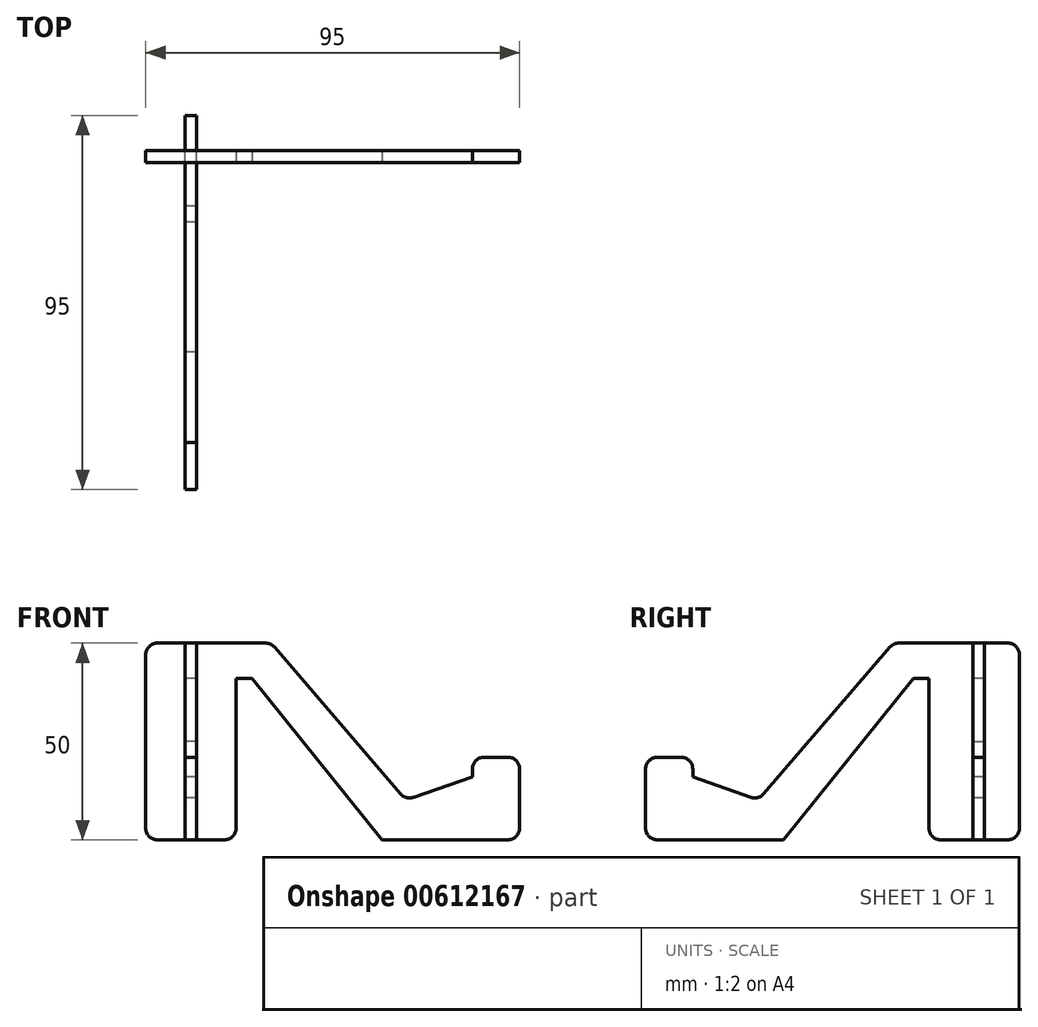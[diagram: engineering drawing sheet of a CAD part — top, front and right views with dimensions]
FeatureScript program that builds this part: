
annotation { "Feature Type Name" : "Feature", "Feature Type Description" : "" }
export const myFeature = defineFeature(function(context is Context, id is Id, definition is map)
    precondition{}
    {
        {
            assignVariable(context, id + "F0", {"name" : "thickness", "anyValue" : 3});
        }
        {
            var Q0;
            Q0=qCreatedBy(makeId("Right.planeOp"),FACE);
            var sketch = newSketch(context, id + "F1", { "sketchPlane" : qUnion([Q0])});
            skLineSegment(sketch, "E0", {"start": v(75, 0) * mm, "end": v(92, 0) * mm});
            skLineSegment(sketch, "E1", {"start": v(95, 3) * mm, "end": v(95, 47) * mm});
            skLineSegment(sketch, "E2", {"start": v(92, 50) * mm, "end": v(86.13, 50) * mm});
            skLineSegment(sketch, "E3", {"start": v(62.1, 48.96) * mm, "end": v(30, 11.67) * mm});
            skLineSegment(sketch, "E4", {"start": v(26.73, 10.8) * mm, "end": v(12, 16) * mm});
            skLineSegment(sketch, "E5", {"start": v(12, 16) * mm, "end": v(12, 18) * mm});
            skLineSegment(sketch, "E6", {"start": v(9, 21) * mm, "end": v(3, 21) * mm});
            skLineSegment(sketch, "E7", {"start": v(0, 18) * mm, "end": v(0, 3) * mm});
            skLineSegment(sketch, "E8", {"start": v(-17.73, 9.3) * mm, "end": v(124.5, 9.3) * mm, "construction": true});
            skLineSegment(sketch, "E9", {"start": v(35, 9.3) * mm, "end": v(35, -14.34) * mm, "construction": true});
            skLineSegment(sketch, "E10", {"start": v(68, 41) * mm, "end": v(72, 41) * mm});
            skLineSegment(sketch, "E11", {"start": v(68, 41) * mm, "end": v(68, 32.72) * mm, "construction": true});
            skLineSegment(sketch, "E12", {"start": v(35, 0) * mm, "end": v(68, 41) * mm});
            skLineSegment(sketch, "E13", {"start": v(72, 41) * mm, "end": v(72, 3) * mm});
            skLineSegment(sketch, "E14.top", {"start": v(83.13, 25) * mm, "end": v(86.13, 25) * mm});
            skLineSegment(sketch, "E14.left", {"start": v(83.13, 50) * mm, "end": v(83.13, 25) * mm});
            skLineSegment(sketch, "E14.right", {"start": v(86.13, 50) * mm, "end": v(86.13, 25) * mm});
            skLineSegment(sketch, "E15", {"start": v(95, 25) * mm, "end": v(77.63, 25) * mm, "construction": true});
            skLineSegment(sketch, "E16.trimOffspring", {"start": v(83.13, 50) * mm, "end": v(64.38, 50) * mm});
            skLineSegment(sketch, "E17.trimOffspring", {"start": v(72, 41) * mm, "end": v(68, 41) * mm, "construction": true});
            skPoint(sketch, "E18.visualSharp", {"position": v(12, 21) * mm});
            skArc(sketch, "E18.filletArc", {"start": v(12, 18) * mm, "mid": v(11.12, 20.12) * mm, "end": v(9, 21) * mm});
            skPoint(sketch, "E19.visualSharp", {"position": v(0, 21) * mm});
            skArc(sketch, "E19.filletArc", {"start": v(3, 21) * mm, "mid": v(0.88, 20.12) * mm, "end": v(0, 18) * mm});
            skPoint(sketch, "E20.visualSharp", {"position": v(0, 0) * mm});
            skArc(sketch, "E20.filletArc", {"start": v(0, 3) * mm, "mid": v(0.88, 0.88) * mm, "end": v(3, 0) * mm});
            skArc(sketch, "E21.filletArc", {"start": v(72, 3) * mm, "mid": v(72.88, 0.88) * mm, "end": v(75, 0) * mm});
            skPoint(sketch, "E22.visualSharp", {"position": v(95, 0) * mm});
            skArc(sketch, "E22.filletArc", {"start": v(92, 0) * mm, "mid": v(94.12, 0.88) * mm, "end": v(95, 3) * mm});
            skPoint(sketch, "E23.visualSharp", {"position": v(95, 50) * mm});
            skArc(sketch, "E23.filletArc", {"start": v(95, 47) * mm, "mid": v(94.12, 49.12) * mm, "end": v(92, 50) * mm});
            skPoint(sketch, "E24.visualSharp", {"position": v(63, 50) * mm});
            skArc(sketch, "E24.filletArc", {"start": v(64.38, 50) * mm, "mid": v(63.13, 49.73) * mm, "end": v(62.1, 48.96) * mm});
            skLineSegment(sketch, "E25", {"start": v(3, 0) * mm, "end": v(35, 0) * mm});
            skPoint(sketch, "E26.visualSharp", {"position": v(28.66, 10.11) * mm});
            skArc(sketch, "E26.filletArc", {"start": v(26.73, 10.8) * mm, "mid": v(28.5, 10.72) * mm, "end": v(30, 11.67) * mm});
            skSolve(sketch);
        }
        {
            var Q0;
            Q0=makeQuery(id+"F1.imprint","IMPRINT",FACE,{"disambiguationData":[TD([[makeQuery(id+"F1.imprint","IMPRINT",EDGE,{"derivedFrom":sQuery(id+"F1.wireOp",EDGE,"E0")}),1.0]])]});
            extrude(context, id + "F2", {"entities" : qUnion([Q0]), "depth" : (getVariable(context, 'thickness')) * mm, "offsetDistance" : 25 * mm});
        }
        {
            var Q0;
            Q0=makeQuery(id+"F2.opExtrude","SWEPT_FACE",FACE,{"disambiguationData":[OSD([sQuery(id+"F1.wireOp",EDGE,"E14.left")])]});
            var sketch = newSketch(context, id + "F3", { "sketchPlane" : qUnion([Q0])});
            skLineSegment(sketch, "E27", {"start": v(-10, 0) * mm, "end": v(7, 0) * mm});
            skLineSegment(sketch, "E28", {"start": v(10, 3) * mm, "end": v(10, 47) * mm});
            skLineSegment(sketch, "E29", {"start": v(7, 50) * mm, "end": v(1.34, 50) * mm});
            skLineSegment(sketch, "E30", {"start": v(-22.69, 48.96) * mm, "end": v(-54.79, 11.67) * mm});
            skLineSegment(sketch, "E31", {"start": v(-58.05, 10.8) * mm, "end": v(-73, 16) * mm});
            skLineSegment(sketch, "E32", {"start": v(-73, 16) * mm, "end": v(-73, 18) * mm});
            skLineSegment(sketch, "E33", {"start": v(-76, 21) * mm, "end": v(-82, 21) * mm});
            skLineSegment(sketch, "E34", {"start": v(-85, 18) * mm, "end": v(-85, 3) * mm});
            skLineSegment(sketch, "E35", {"start": v(-102.73, 9.3) * mm, "end": v(39.5, 9.3) * mm, "construction": true});
            skLineSegment(sketch, "E36", {"start": v(-50, 9.3) * mm, "end": v(-50, -14.34) * mm, "construction": true});
            skLineSegment(sketch, "E37", {"start": v(-17, 41) * mm, "end": v(-13, 41) * mm});
            skLineSegment(sketch, "E38", {"start": v(-17, 41) * mm, "end": v(-17, 32.72) * mm, "construction": true});
            skLineSegment(sketch, "E39", {"start": v(-50, 0) * mm, "end": v(-17, 41) * mm});
            skLineSegment(sketch, "E40", {"start": v(-13, 41) * mm, "end": v(-13, 3) * mm});
            skLineSegment(sketch, "E41.trimOffspring", {"start": v(1.34, 50) * mm, "end": v(-20.42, 50) * mm});
            skLineSegment(sketch, "E42.trimOffspring", {"start": v(-13, 41) * mm, "end": v(-17, 41) * mm, "construction": true});
            skPoint(sketch, "E43.visualSharp", {"position": v(-73, 21) * mm});
            skArc(sketch, "E43.filletArc", {"start": v(-73, 18) * mm, "mid": v(-73.88, 20.12) * mm, "end": v(-76, 21) * mm});
            skPoint(sketch, "E44.visualSharp", {"position": v(-85, 21) * mm});
            skArc(sketch, "E44.filletArc", {"start": v(-82, 21) * mm, "mid": v(-84.12, 20.12) * mm, "end": v(-85, 18) * mm});
            skPoint(sketch, "E45.visualSharp", {"position": v(-85, 0) * mm});
            skArc(sketch, "E45.filletArc", {"start": v(-85, 3) * mm, "mid": v(-84.12, 0.88) * mm, "end": v(-82, 0) * mm});
            skArc(sketch, "E46.filletArc", {"start": v(-13, 3) * mm, "mid": v(-12.12, 0.88) * mm, "end": v(-10, 0) * mm});
            skPoint(sketch, "E47.visualSharp", {"position": v(10, 0) * mm});
            skArc(sketch, "E47.filletArc", {"start": v(7, 0) * mm, "mid": v(9.12, 0.88) * mm, "end": v(10, 3) * mm});
            skPoint(sketch, "E48.visualSharp", {"position": v(10, 50) * mm});
            skArc(sketch, "E48.filletArc", {"start": v(10, 47) * mm, "mid": v(9.12, 49.12) * mm, "end": v(7, 50) * mm});
            skPoint(sketch, "E49.visualSharp", {"position": v(-21.8, 50) * mm});
            skArc(sketch, "E49.filletArc", {"start": v(-20.42, 50) * mm, "mid": v(-21.67, 49.73) * mm, "end": v(-22.69, 48.96) * mm});
            skLineSegment(sketch, "E50", {"start": v(-82, 0) * mm, "end": v(-50, 0) * mm});
            skPoint(sketch, "E51.visualSharp", {"position": v(-56.12, 10.12) * mm});
            skArc(sketch, "E51.filletArc", {"start": v(-58.05, 10.8) * mm, "mid": v(-56.28, 10.73) * mm, "end": v(-54.79, 11.67) * mm});
            skLineSegment(sketch, "E52", {"start": v(-13, 18.9) * mm, "end": v(10, 18.9) * mm, "construction": true});
            skLineSegment(sketch, "E53", {"start": v(10, 18.9) * mm, "end": v(-1.5, 18.9) * mm, "construction": true});
            skLineSegment(sketch, "E54", {"start": v(-1.5, 18.9) * mm, "end": v(-1.5, 60.17) * mm, "construction": true});
            skLineSegment(sketch, "E55", {"start": v(-3, 47) * mm, "end": v(-3, 63.53) * mm, "construction": true});
            skLineSegment(sketch, "E56", {"start": v(-3, 57.22) * mm, "end": v(0, 57.22) * mm, "construction": true});
            skLineSegment(sketch, "E57", {"start": v(-1.5, 57.22) * mm, "end": v(-1.5, 60.17) * mm, "construction": true});
            skSolve(sketch);
        }
        {
            var Q0;
            Q0=makeQuery(id+"F3.imprint","IMPRINT",FACE,{"disambiguationData":[TD([[makeQuery(id+"F3.imprint","IMPRINT",EDGE,{"derivedFrom":sQuery(id+"F3.wireOp",EDGE,"E27")}),1.0]])]});
            var Q1;
            {var subQ1=sQuery(id+"F1.wireOp",EDGE,"E14.left");var subQ2=makeQuery(id+"F2.opExtrude","CAP_EDGE",EDGE,{"disambiguationData":[OSD([subQ1])],"isStart":true});Q1=makeQuery(id+"F3.imprint","IMPRINT",FACE,{"disambiguationData":[TD([[makeQuery(id+"F3.imprint","IMPRINT",EDGE,{"derivedFrom":subQ2}),-1.0]])]});}
            extrude(context, id + "F4", {"entities" : qUnion([Q0, Q1]), "depth" : (getVariable(context, 'thickness')) * mm, "offsetDistance" : 25 * mm});
        }
        {
            var Q0;
            Q0=makeQuery(id+"F2.opExtrude","SWEPT_BODY",BODY,{"disambiguationData":[OSD([sQuery(id+"F1.wireOp",EDGE,"E0"),sQuery(id+"F1.wireOp",EDGE,"E1"),sQuery(id+"F1.wireOp",EDGE,"E2"),sQuery(id+"F1.wireOp",EDGE,"E3"),sQuery(id+"F1.wireOp",EDGE,"E4"),sQuery(id+"F1.wireOp",EDGE,"E5"),sQuery(id+"F1.wireOp",EDGE,"E6"),sQuery(id+"F1.wireOp",EDGE,"E7"),sQuery(id+"F1.wireOp",EDGE,"E10"),sQuery(id+"F1.wireOp",EDGE,"E12"),sQuery(id+"F1.wireOp",EDGE,"E13"),sQuery(id+"F1.wireOp",EDGE,"E14.top"),sQuery(id+"F1.wireOp",EDGE,"E14.left"),sQuery(id+"F1.wireOp",EDGE,"E14.right"),sQuery(id+"F1.wireOp",EDGE,"E16.trimOffspring"),sQuery(id+"F1.wireOp",EDGE,"E18.filletArc"),sQuery(id+"F1.wireOp",EDGE,"E19.filletArc"),sQuery(id+"F1.wireOp",EDGE,"E20.filletArc"),sQuery(id+"F1.wireOp",EDGE,"E21.filletArc"),sQuery(id+"F1.wireOp",EDGE,"E22.filletArc"),sQuery(id+"F1.wireOp",EDGE,"E23.filletArc"),sQuery(id+"F1.wireOp",EDGE,"E24.filletArc"),sQuery(id+"F1.wireOp",EDGE,"E25"),sQuery(id+"F1.wireOp",EDGE,"E26.filletArc")])]});
            var Q1;
            Q1=makeQuery(id+"F4.opExtrude","SWEPT_BODY",BODY,{"disambiguationData":[OSD([sQuery(id+"F3.wireOp",EDGE,"E27"),sQuery(id+"F3.wireOp",EDGE,"E28"),sQuery(id+"F3.wireOp",EDGE,"E29"),sQuery(id+"F3.wireOp",EDGE,"E30"),sQuery(id+"F3.wireOp",EDGE,"E31"),sQuery(id+"F3.wireOp",EDGE,"E32"),sQuery(id+"F3.wireOp",EDGE,"E33"),sQuery(id+"F3.wireOp",EDGE,"E34"),sQuery(id+"F3.wireOp",EDGE,"E37"),sQuery(id+"F3.wireOp",EDGE,"E39"),sQuery(id+"F3.wireOp",EDGE,"E40"),sQuery(id+"F3.wireOp",EDGE,"E41.trimOffspring"),sQuery(id+"F3.wireOp",EDGE,"E43.filletArc"),sQuery(id+"F3.wireOp",EDGE,"E44.filletArc"),sQuery(id+"F3.wireOp",EDGE,"E45.filletArc"),sQuery(id+"F3.wireOp",EDGE,"E46.filletArc"),sQuery(id+"F3.wireOp",EDGE,"E47.filletArc"),sQuery(id+"F3.wireOp",EDGE,"E48.filletArc"),sQuery(id+"F3.wireOp",EDGE,"E49.filletArc"),sQuery(id+"F3.wireOp",EDGE,"E50"),sQuery(id+"F3.wireOp",EDGE,"E51.filletArc")])]});
            booleanBodies(context, id + "F5", {"operationType" : BooleanOperationType.SUBTRACTION, "tools" : qUnion([Q0]), "targets" : qUnion([Q1]), "keepTools" : true});
        }
    });
